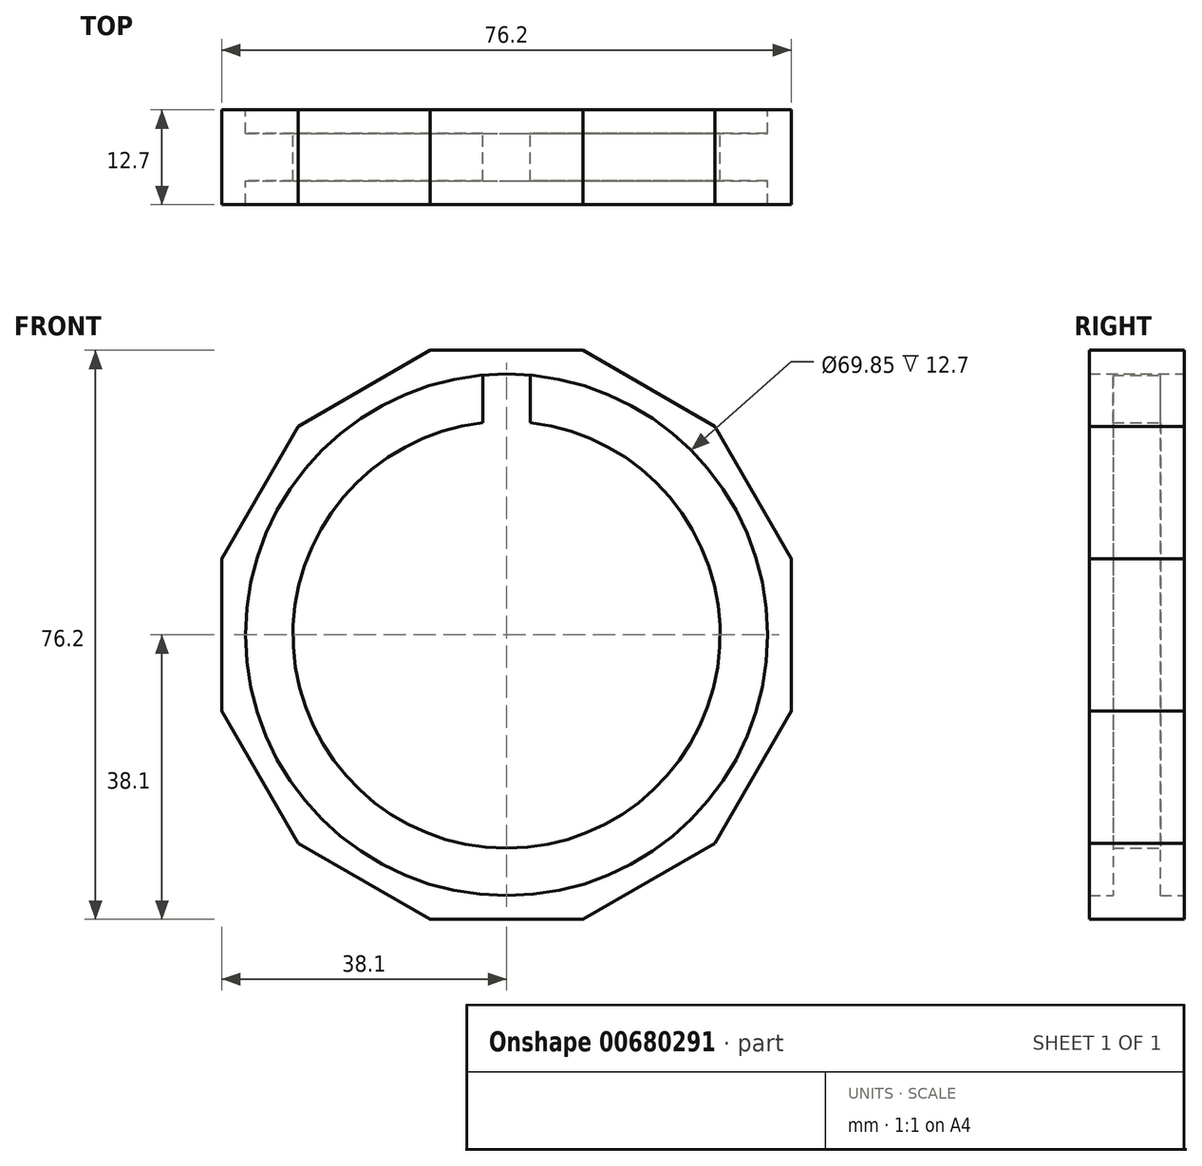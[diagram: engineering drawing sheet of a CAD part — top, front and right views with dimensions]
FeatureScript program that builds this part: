
annotation { "Feature Type Name" : "Feature", "Feature Type Description" : "" }
export const myFeature = defineFeature(function(context is Context, id is Id, definition is map)
    precondition{}
    {
        {
            var Q0;
            Q0=qCreatedBy(makeId("Front.planeOp"),FACE);
            var sketch = newSketch(context, id + "F0", { "sketchPlane" : qUnion([Q0])});
            skCircle(sketch, "E0.cCircle", {"center": v(0, 0) * mm, "radius": 38.1 * mm, "construction": true});
            skLineSegment(sketch, "E0.0", {"start": v(10.2, 38.1) * mm, "end": v(27.9, 27.9) * mm});
            skLineSegment(sketch, "E0.1", {"start": v(27.9, 27.9) * mm, "end": v(38.1, 10.2) * mm});
            skLineSegment(sketch, "E0.2", {"start": v(38.1, 10.2) * mm, "end": v(38.1, -10.2) * mm});
            skLineSegment(sketch, "E0.3", {"start": v(38.1, -10.2) * mm, "end": v(27.9, -27.9) * mm});
            skLineSegment(sketch, "E0.4", {"start": v(27.9, -27.9) * mm, "end": v(10.2, -38.1) * mm});
            skLineSegment(sketch, "E0.5", {"start": v(10.2, -38.1) * mm, "end": v(-10.2, -38.1) * mm});
            skLineSegment(sketch, "E0.6", {"start": v(-10.2, -38.1) * mm, "end": v(-27.9, -27.9) * mm});
            skLineSegment(sketch, "E0.7", {"start": v(-27.9, -27.9) * mm, "end": v(-38.1, -10.2) * mm});
            skLineSegment(sketch, "E0.8", {"start": v(-38.1, -10.2) * mm, "end": v(-38.1, 10.2) * mm});
            skLineSegment(sketch, "E0.9", {"start": v(-38.1, 10.2) * mm, "end": v(-27.9, 27.9) * mm});
            skLineSegment(sketch, "E0.10", {"start": v(-27.9, 27.9) * mm, "end": v(-10.2, 38.1) * mm});
            skLineSegment(sketch, "E0.11", {"start": v(-10.2, 38.1) * mm, "end": v(10.2, 38.1) * mm});
            skPoint(sketch, "E0.0.midPoint", {"position": v(19.05, 33) * mm});
            skCircle(sketch, "E1", {"center": v(0, 0) * mm, "radius": 34.93 * mm});
            skSolve(sketch);
        }
        {
            var Q0;
            Q0 = qSketchRegion(id + "F0", true);
            extrude(context, id + "F1", {"entities" : qUnion([Q0]), "endBound" : BoundingType.SYMMETRIC, "depth" : 12.7 * mm, "offsetDistance" : 25.4 * mm});
        }
        {
            var Q0;
            Q0=qCreatedBy(makeId("Front.planeOp"),FACE);
            var sketch = newSketch(context, id + "F2", { "sketchPlane" : qUnion([Q0])});
            skArc(sketch, "E2", {"start": v(-3.17, 34.78) * mm, "mid": v(0, -34.93) * mm, "end": v(3.18, 34.78) * mm});
            skArc(sketch, "E3", {"start": v(-3.17, 28.4) * mm, "mid": v(0, -28.57) * mm, "end": v(3.18, 28.4) * mm});
            skLineSegment(sketch, "E4.bottom", {"start": v(-3.17, 20.49) * mm, "end": v(3.18, 20.49) * mm, "construction": true});
            skLineSegment(sketch, "E4.top", {"start": v(-3.18, 50.8) * mm, "end": v(3.17, 50.8) * mm, "construction": true});
            skLineSegment(sketch, "E4.left", {"start": v(-3.17, 20.49) * mm, "end": v(-3.18, 50.8) * mm, "construction": true});
            skLineSegment(sketch, "E4.right", {"start": v(3.18, 20.49) * mm, "end": v(3.17, 50.8) * mm, "construction": true});
            skLineSegment(sketch, "E5", {"start": v(-3.17, 28.4) * mm, "end": v(-3.17, 34.78) * mm});
            skLineSegment(sketch, "E6", {"start": v(3.18, 28.4) * mm, "end": v(3.17, 34.78) * mm});
            skSolve(sketch);
        }
        {
            var Q0;
            Q0 = qSketchRegion(id + "F2", true);
            extrude(context, id + "F3", {"entities" : qUnion([Q0]), "operationType" : NewBodyOperationType.ADD, "endBound" : BoundingType.SYMMETRIC, "depth" : 6.35 * mm, "offsetDistance" : 25.4 * mm});
        }
    });
